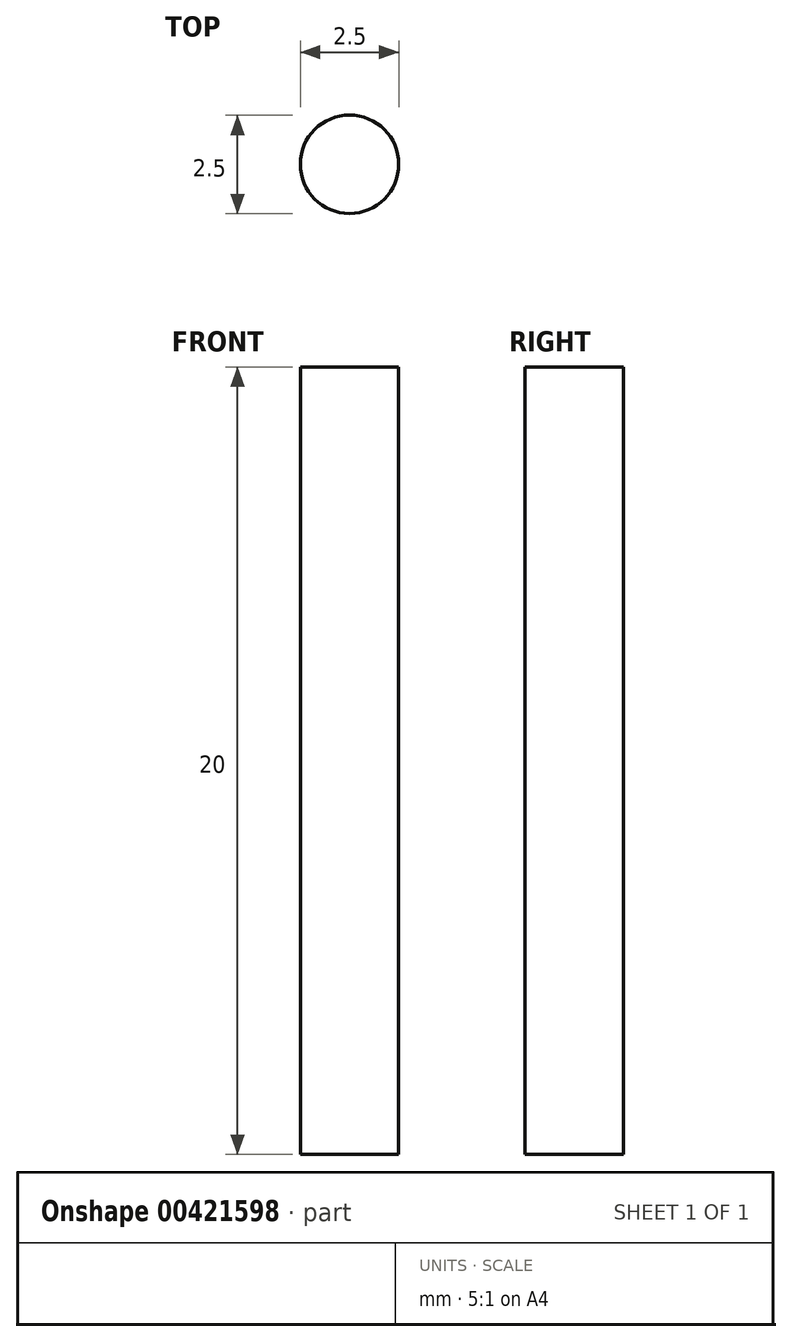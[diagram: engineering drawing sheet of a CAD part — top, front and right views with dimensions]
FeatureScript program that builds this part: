
annotation { "Feature Type Name" : "Feature", "Feature Type Description" : "" }
export const myFeature = defineFeature(function(context is Context, id is Id, definition is map)
    precondition{}
    {
        {
            var Q0;
            Q0=qCreatedBy(makeId("Top.planeOp"),FACE);
            var sketch = newSketch(context, id + "F0", { "sketchPlane" : qUnion([Q0])});
            skCircle(sketch, "E0", {"center": v(-42.67, -22.64) * mm, "radius": 1.25 * mm});
            skSolve(sketch);
        }
        {
            var Q0;
            Q0 = qSketchRegion(id + "F0", true);
            extrude(context, id + "F1", {"entities" : qUnion([Q0]), "depth" : 20 * mm, "offsetDistance" : 25 * mm});
        }
    });
